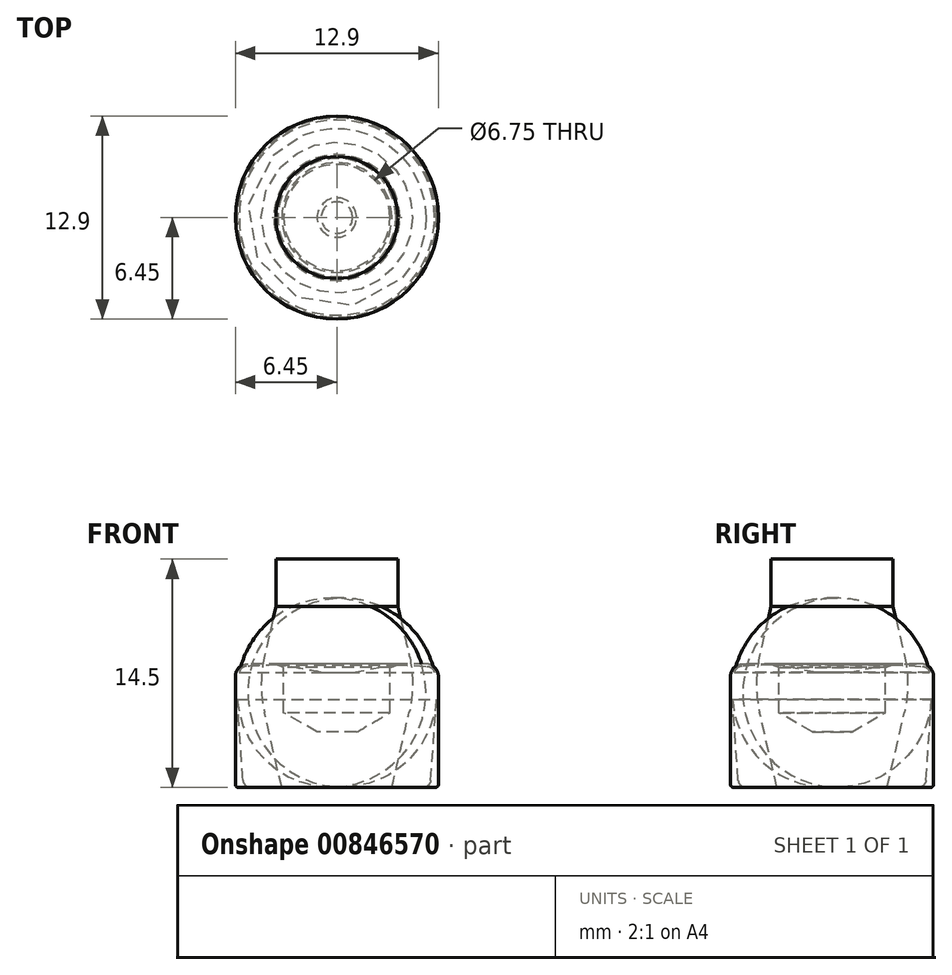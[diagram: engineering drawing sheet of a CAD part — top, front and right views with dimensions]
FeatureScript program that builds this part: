
annotation { "Feature Type Name" : "Feature", "Feature Type Description" : "" }
export const myFeature = defineFeature(function(context is Context, id is Id, definition is map)
    precondition{}
    {
        {
            var Q0;
            Q0=qCreatedBy(makeId("Front.planeOp"),FACE);
            var sketch = newSketch(context, id + "F0", { "sketchPlane" : qUnion([Q0])});
            skLineSegment(sketch, "E0", {"start": v(0, 0) * mm, "end": v(0, 3.52) * mm, "construction": true});
            skLineSegment(sketch, "E1", {"start": v(3.37, 7.85) * mm, "end": v(5.65, 7.85) * mm});
            skLineSegment(sketch, "E2", {"start": v(6.45, 7.05) * mm, "end": v(6.45, 0.2) * mm});
            skLineSegment(sketch, "E3", {"start": v(6.25, 0) * mm, "end": v(0, 0) * mm});
            skPoint(sketch, "E4.visualSharp", {"position": v(6.45, 7.85) * mm});
            skArc(sketch, "E4.filletArc", {"start": v(6.45, 7.05) * mm, "mid": v(6.22, 7.62) * mm, "end": v(5.65, 7.85) * mm});
            skPoint(sketch, "E5.visualSharp", {"position": v(6.45, 0) * mm});
            skArc(sketch, "E5.filletArc", {"start": v(6.25, 0) * mm, "mid": v(6.4, 0.06) * mm, "end": v(6.45, 0.2) * mm});
            skLineSegment(sketch, "E6", {"start": v(3.37, 7.85) * mm, "end": v(3.38, 4.75) * mm});
            skLineSegment(sketch, "E7", {"start": v(3.38, 4.75) * mm, "end": v(1.25, 3.52) * mm});
            skLineSegment(sketch, "E8", {"start": v(1.25, 3.52) * mm, "end": v(0, 3.52) * mm});
            skLineSegment(sketch, "E9", {"start": v(0, 3.52) * mm, "end": v(0, 0) * mm});
            skSolve(sketch);
        }
        {
            var Q0;
            Q0=qSketchRegion(id+"F0",true);
            var Q1;
            Q1=sQuery(id+"F0.wireOp",EDGE,"E9");
            revolve(context, id + "F1", {"entities" : qUnion([Q0]), "axis" : qUnion([Q1]), "revolveType" : RevolveType.FULL});
        }
        {
            var Q0;
            Q0=makeQuery(id+"F1.opRevolve","SWEPT_FACE",FACE,{"disambiguationData":[OSD([sQuery(id+"F0.wireOp",EDGE,"E1")])]});
            var sketch = newSketch(context, id + "F2", { "sketchPlane" : qUnion([Q0])});
            skArc(sketch, "E10", {"start": v(0.65, 2.87) * mm, "mid": v(0, 3.37) * mm, "end": v(-0.65, 2.87) * mm});
            skLineSegment(sketch, "E11", {"start": v(-0.65, 2.87) * mm, "end": v(-0.67, 2.82) * mm});
            skLineSegment(sketch, "E12", {"start": v(0.65, 2.87) * mm, "end": v(0.67, 2.82) * mm});
            skLineSegment(sketch, "E13.1.0", {"start": v(-2.16, 2) * mm, "end": v(-2.11, 1.99) * mm});
            skArc(sketch, "E13.1.1", {"start": v(-2.16, 2) * mm, "mid": v(-2.92, 1.69) * mm, "end": v(-2.82, 0.87) * mm});
            skLineSegment(sketch, "E13.1.2", {"start": v(-2.82, 0.87) * mm, "end": v(-2.78, 0.84) * mm});
            skLineSegment(sketch, "E13.2.0", {"start": v(-2.82, -0.87) * mm, "end": v(-2.78, -0.84) * mm});
            skArc(sketch, "E13.2.1", {"start": v(-2.82, -0.87) * mm, "mid": v(-2.92, -1.69) * mm, "end": v(-2.16, -2) * mm});
            skLineSegment(sketch, "E13.2.2", {"start": v(-2.16, -2) * mm, "end": v(-2.11, -1.99) * mm});
            skLineSegment(sketch, "E13.3.0", {"start": v(-0.65, -2.87) * mm, "end": v(-0.67, -2.82) * mm});
            skArc(sketch, "E13.3.1", {"start": v(-0.65, -2.87) * mm, "mid": v(0, -3.37) * mm, "end": v(0.65, -2.87) * mm});
            skLineSegment(sketch, "E13.3.2", {"start": v(0.65, -2.87) * mm, "end": v(0.67, -2.82) * mm});
            skLineSegment(sketch, "E13.4.0", {"start": v(2.16, -2) * mm, "end": v(2.11, -1.99) * mm});
            skArc(sketch, "E13.4.1", {"start": v(2.16, -2) * mm, "mid": v(2.92, -1.69) * mm, "end": v(2.82, -0.87) * mm});
            skLineSegment(sketch, "E13.4.2", {"start": v(2.82, -0.87) * mm, "end": v(2.78, -0.84) * mm});
            skLineSegment(sketch, "E13.5.0", {"start": v(2.82, 0.87) * mm, "end": v(2.78, 0.84) * mm});
            skArc(sketch, "E13.5.1", {"start": v(2.82, 0.87) * mm, "mid": v(2.92, 1.69) * mm, "end": v(2.16, 2) * mm});
            skLineSegment(sketch, "E13.5.2", {"start": v(2.16, 2) * mm, "end": v(2.11, 1.99) * mm});
            skPoint(sketch, "E13.center", {"position": v(0, 0) * mm});
            skPoint(sketch, "E14.newPointA", {"position": v(0.6, 1.26) * mm});
            skPoint(sketch, "E14.newPointB", {"position": v(-1.4, 0.1) * mm});
            skArc(sketch, "E14.filletArc", {"start": v(-2.11, 1.99) * mm, "mid": v(-1.22, 2.1) * mm, "end": v(-0.67, 2.82) * mm});
            skPoint(sketch, "E15.newPointA", {"position": v(-0.6, 1.26) * mm});
            skPoint(sketch, "E15.newPointB", {"position": v(1.4, 0.12) * mm});
            skArc(sketch, "E15.filletArc", {"start": v(0.67, 2.82) * mm, "mid": v(1.22, 2.1) * mm, "end": v(2.11, 1.99) * mm});
            skPoint(sketch, "E16.newPointA", {"position": v(0.8, -1.15) * mm});
            skPoint(sketch, "E16.newPointB", {"position": v(0.8, 1.15) * mm});
            skArc(sketch, "E16.filletArc", {"start": v(2.78, 0.84) * mm, "mid": v(2.43, 0) * mm, "end": v(2.78, -0.84) * mm});
            skPoint(sketch, "E17.newPointA", {"position": v(-0.6, -1.26) * mm});
            skPoint(sketch, "E17.newPointB", {"position": v(1.4, -0.1) * mm});
            skArc(sketch, "E17.filletArc", {"start": v(2.11, -1.99) * mm, "mid": v(1.22, -2.1) * mm, "end": v(0.67, -2.82) * mm});
            skPoint(sketch, "E18.newPointA", {"position": v(-1.4, -0.12) * mm});
            skPoint(sketch, "E18.newPointB", {"position": v(0.6, -1.26) * mm});
            skArc(sketch, "E18.filletArc", {"start": v(-0.67, -2.82) * mm, "mid": v(-1.22, -2.1) * mm, "end": v(-2.11, -1.99) * mm});
            skPoint(sketch, "E19.newPointA", {"position": v(-0.8, 1.15) * mm});
            skPoint(sketch, "E19.newPointB", {"position": v(-0.8, -1.15) * mm});
            skArc(sketch, "E19.filletArc", {"start": v(-2.78, -0.84) * mm, "mid": v(-2.43, 0) * mm, "end": v(-2.78, 0.84) * mm});
            skCircle(sketch, "E20", {"center": v(0, 0) * mm, "radius": 3.61 * mm});
            skSolve(sketch);
        }
        {
            var Q0;
            Q0=makeQuery(id+"FIAhyzxjR6a7Dz0_1.boolean.opBoolean","MERGE",FACE,{"derivedFrom":[makeQuery(id+"F1.opRevolve","SWEPT_FACE",FACE,{"disambiguationData":[OSD([sQuery(id+"F0.wireOp",EDGE,"E1")])]}),makeQuery(id+"FIAhyzxjR6a7Dz0_1.opExtrude","CAP_FACE",FACE,{"disambiguationData":[OSD([sQuery(id+"F2.wireOp",EDGE,"E10"),sQuery(id+"F2.wireOp",EDGE,"E11"),sQuery(id+"F2.wireOp",EDGE,"E12"),sQuery(id+"F2.wireOp",EDGE,"E13.1.0"),sQuery(id+"F2.wireOp",EDGE,"E13.1.1"),sQuery(id+"F2.wireOp",EDGE,"E13.1.2"),sQuery(id+"F2.wireOp",EDGE,"E13.2.0"),sQuery(id+"F2.wireOp",EDGE,"E13.2.1"),sQuery(id+"F2.wireOp",EDGE,"E13.2.2"),sQuery(id+"F2.wireOp",EDGE,"E13.3.0"),sQuery(id+"F2.wireOp",EDGE,"E13.3.1"),sQuery(id+"F2.wireOp",EDGE,"E13.3.2"),sQuery(id+"F2.wireOp",EDGE,"E13.4.0"),sQuery(id+"F2.wireOp",EDGE,"E13.4.1"),sQuery(id+"F2.wireOp",EDGE,"E13.4.2"),sQuery(id+"F2.wireOp",EDGE,"E13.5.0"),sQuery(id+"F2.wireOp",EDGE,"E13.5.1"),sQuery(id+"F2.wireOp",EDGE,"E13.5.2"),sQuery(id+"F2.wireOp",EDGE,"E14.filletArc"),sQuery(id+"F2.wireOp",EDGE,"E15.filletArc"),sQuery(id+"F2.wireOp",EDGE,"E16.filletArc"),sQuery(id+"F2.wireOp",EDGE,"E17.filletArc"),sQuery(id+"F2.wireOp",EDGE,"E18.filletArc"),sQuery(id+"F2.wireOp",EDGE,"E19.filletArc"),sQuery(id+"F2.wireOp",EDGE,"E20")])],"isStart":true})]});
            var sketch = newSketch(context, id + "F3", { "sketchPlane" : qUnion([Q0])});
            skCircle(sketch, "E21", {"center": v(0, 0) * mm, "radius": 4 * mm});
            skSolve(sketch);
        }
        {
            var Q0;
            Q0=qSketchRegion(id+"F3",true);
            extrude(context, id + "F4", {"entities" : qUnion([Q0]), "operationType" : NewBodyOperationType.REMOVE, "oppositeDirection" : true, "depth" : 1 * mm, "hasDraft" : true, "draftAngle" : 70 * degree, "draftPullDirection" : true});
        }
        {
            var Q0;
            Q0=qCreatedBy(makeId("Front.planeOp"),FACE);
            var sketch = newSketch(context, id + "F5", { "sketchPlane" : qUnion([Q0])});
            skLineSegment(sketch, "E22", {"start": v(0, 0) * mm, "end": v(0, 14.5) * mm, "construction": true});
            skLineSegment(sketch, "E23", {"start": v(0, 14.5) * mm, "end": v(3.87, 14.5) * mm});
            skLineSegment(sketch, "E24", {"start": v(3.87, 14.5) * mm, "end": v(3.87, 11.5) * mm});
            skLineSegment(sketch, "E25", {"start": v(3.87, 11.5) * mm, "end": v(4.6, 8.37) * mm});
            skLineSegment(sketch, "E26", {"start": v(3.5, 0) * mm, "end": v(0, 0) * mm});
            skLineSegment(sketch, "E27", {"start": v(0, 14.5) * mm, "end": v(0, 0) * mm});
            skLineSegment(sketch, "E28", {"start": v(3.5, 0) * mm, "end": v(4.6, 4.77) * mm});
            skArc(sketch, "E29.filletArc", {"start": v(4.6, 4.77) * mm, "mid": v(4.8, 6.57) * mm, "end": v(4.6, 8.37) * mm});
            skSolve(sketch);
        }
        {
            var Q0;
            Q0=qSketchRegion(id+"F5",true);
            var Q1;
            Q1=sQuery(id+"F5.wireOp",EDGE,"E27");
            revolve(context, id + "F6", {"entities" : qUnion([Q0]), "axis" : qUnion([Q1]), "revolveType" : RevolveType.FULL});
        }
        {
            var Q0;
            Q0=qCreatedBy(makeId("Front.planeOp"),FACE);
            var sketch = newSketch(context, id + "F7", { "sketchPlane" : qUnion([Q0])});
            skLineSegment(sketch, "E30", {"start": v(0, 0) * mm, "end": v(0, 7.32) * mm});
            skLineSegment(sketch, "E31", {"start": v(6.32, 5.6) * mm, "end": v(5.96, 0.47) * mm});
            skLineSegment(sketch, "E32", {"start": v(5.46, 0) * mm, "end": v(0, 0) * mm});
            skPoint(sketch, "E33.visualSharp", {"position": v(5.93, 0) * mm});
            skArc(sketch, "E33.filletArc", {"start": v(5.46, 0) * mm, "mid": v(5.8, 0.13) * mm, "end": v(5.96, 0.47) * mm});
            skLineSegment(sketch, "E34", {"start": v(0, 7.32) * mm, "end": v(0, 0) * mm, "construction": true});
            skLineSegment(sketch, "E35", {"start": v(0, 7.32) * mm, "end": v(1, 7.32) * mm});
            skLineSegment(sketch, "E36", {"start": v(1, 7.32) * mm, "end": v(3.75, 7.8) * mm});
            skLineSegment(sketch, "E37", {"start": v(3.75, 7.8) * mm, "end": v(5.74, 7.7) * mm});
            skArc(sketch, "E38.filletArc", {"start": v(6.32, 5.6) * mm, "mid": v(6.32, 6.46) * mm, "end": v(6.2, 7.3) * mm});
            skPoint(sketch, "E39.visualSharp", {"position": v(6.1, 7.68) * mm});
            skArc(sketch, "E39.filletArc", {"start": v(6.2, 7.3) * mm, "mid": v(6.04, 7.58) * mm, "end": v(5.74, 7.7) * mm});
            skLineSegment(sketch, "E40", {"start": v(6.32, 5.6) * mm, "end": v(6.35, 6) * mm, "construction": true});
            skSolve(sketch);
        }
        {
            var Q0;
            Q0=qSketchRegion(id+"F7",true);
            var Q1;
            Q1=sQuery(id+"F7.wireOp",EDGE,"E30");
            revolve(context, id + "F8", {"entities" : qUnion([Q0]), "axis" : qUnion([Q1]), "revolveType" : RevolveType.FULL});
        }
    });
